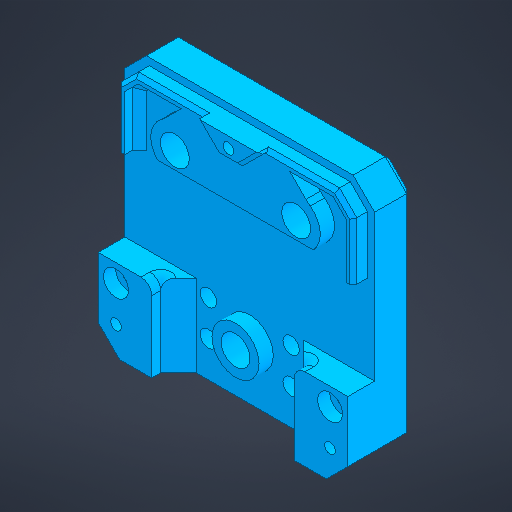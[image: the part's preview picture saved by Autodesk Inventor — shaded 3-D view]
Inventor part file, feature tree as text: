
AUTODESK INVENTOR PART (.ipt)
format: ipt  version: 2025.1 (Build 291241000, 241)  size: 1,003,520 bytes
history: native  units: mm
features: extrude x13, sketch x5, chamfer x5, fillet x2, mirror x1, plane x1
ambient origin geometry x8: Origin, YZ Plane, XZ Plane, XY Plane, X Axis, Y Axis, Z Axis, Center Point
bodies: Solid1 (feature_tree)
feature tree (27):
  sketch  "Sketch1"  dims[d6=40.0mm d7=34.0mm d8=24.0mm d9=24.0mm d10=24.0mm d11=70.0mm d12=70.0mm d14=6.0mm d15=6.0mm d16=6.0mm d17=6.0mm d18=10.0mm]
  extrude  "Extrusion1"  Depth=10.0mm
  extrude  "Extrusion2"  Depth=15.0mm
  extrude  "Extrusion3"  Depth=10.0mm
  extrude  "Extrusion4"  Depth=8.0mm
  extrude  "Extrusion10"  Depth=4.0mm
  extrude  "Extrusion7"  Depth=4.0mm
  extrude  "Extrusion6"  TaperAngle=45.0deg  [1 undecoded]
  mirror  "Mirror1"
  fillet  "Fillet1"  Radius=5.0mm
  sketch  "Sketch2"  dims[d19=20.0mm d20=15.0mm]
  extrude  "Extrusion11"  Depth=7.0mm
  extrude  "Extrusion15"  Depth=7.0mm
  chamfer  "Chamfer2"  Distance=7.0mm
  chamfer  "Chamfer3"  Distance=11.0mm
  sketch  "Sketch4"  dims[d21=12.0mm d22=10.0mm]
  plane  "Work Plane1"
  extrude  "Extrusion13"  Depth=4.0mm
  extrude  "Extrusion12"  Depth=4.0mm
  chamfer  "Chamfer5"  Distance=4.0mm
  fillet  "Fillet2"  Radius=5.5mm
  extrude  "Extrusion16"  Depth=11.0mm
  chamfer  "Chamfer6"  Distance=11.0mm
  chamfer  "Chamfer1"  Distance=4.0mm
  extrude  "Extrusion17"  Depth=4.0mm
  sketch  "Sketch5"  dims[d23=8.0mm d24=3.0mm]
  sketch  "Sketch6"  dims[d25=3.0mm d26=5.0mm d27=3.0mm d29=45.0deg d31=5.0mm d32=7.0mm d33=7.0mm d34=7.0mm d35=11.0mm d36=0.0mm d37=5.5mm d38=4.0mm d40=4.0mm d41=5.5mm d42=11.0mm d43=11.0mm d44=4.0mm d45=0.0mm d46=5.2mm d47=4.0mm d48=11.0mm d49=2.0mm d50=0.0mm d51=7.5mm d52=0.0mm d55=10.0mm d56=0.0mm d57=0.0mm d58=8.8mm d59=0.0mm d60=8.0mm d61=8.0mm d62=8.0mm d67=3.4mm d68=0.0mm d69=4.0mm d70=2.0mm d71=45.0deg d72=8.8mm d73=0.0mm d74=3.0mm d75=3.0mm d76=2.0mm d77=2.0mm d78=2.0mm d79=2.0mm d80=2.0mm d81=2.0mm d82=12.0mm d83=2.0mm d84=2.0mm d85=2.0mm d86=2.0mm d87=2.0mm d88=2.0mm d89=1.0mm d90=2.0mm d91=45.0deg d92=2.0mm d93=2.0mm d94=45.0deg d98=4.6mm d99=4.6mm d100=4.6mm d101=4.6mm d110=8.0mm d111=0.0mm d112=11.5mm d113=3.4mm d114=50.0mm d115=13.0mm d116=10.0mm d117=0.0mm d118=3.0mm d119=5.7mm d120=5.7mm d121=5.7mm d122=5.7mm d125=6.0mm d126=0.0mm d131=23.2mm d132=10.0mm d134=10.0mm d135=5.0mm d136=2.0mm d137=45.0deg d138=8.1mm d139=6.3mm d140=0.0mm d141=2.0mm d142=2.0mm d143=45.0deg d145=4.0mm d146=0.0mm d147=2.0mm d148=0.872665mm]
note: 1 required parameter value undecoded (feature->parameter linkage not recoverable at this tier; creation-order binding heuristic only, values carry confidence <= 0.55)
